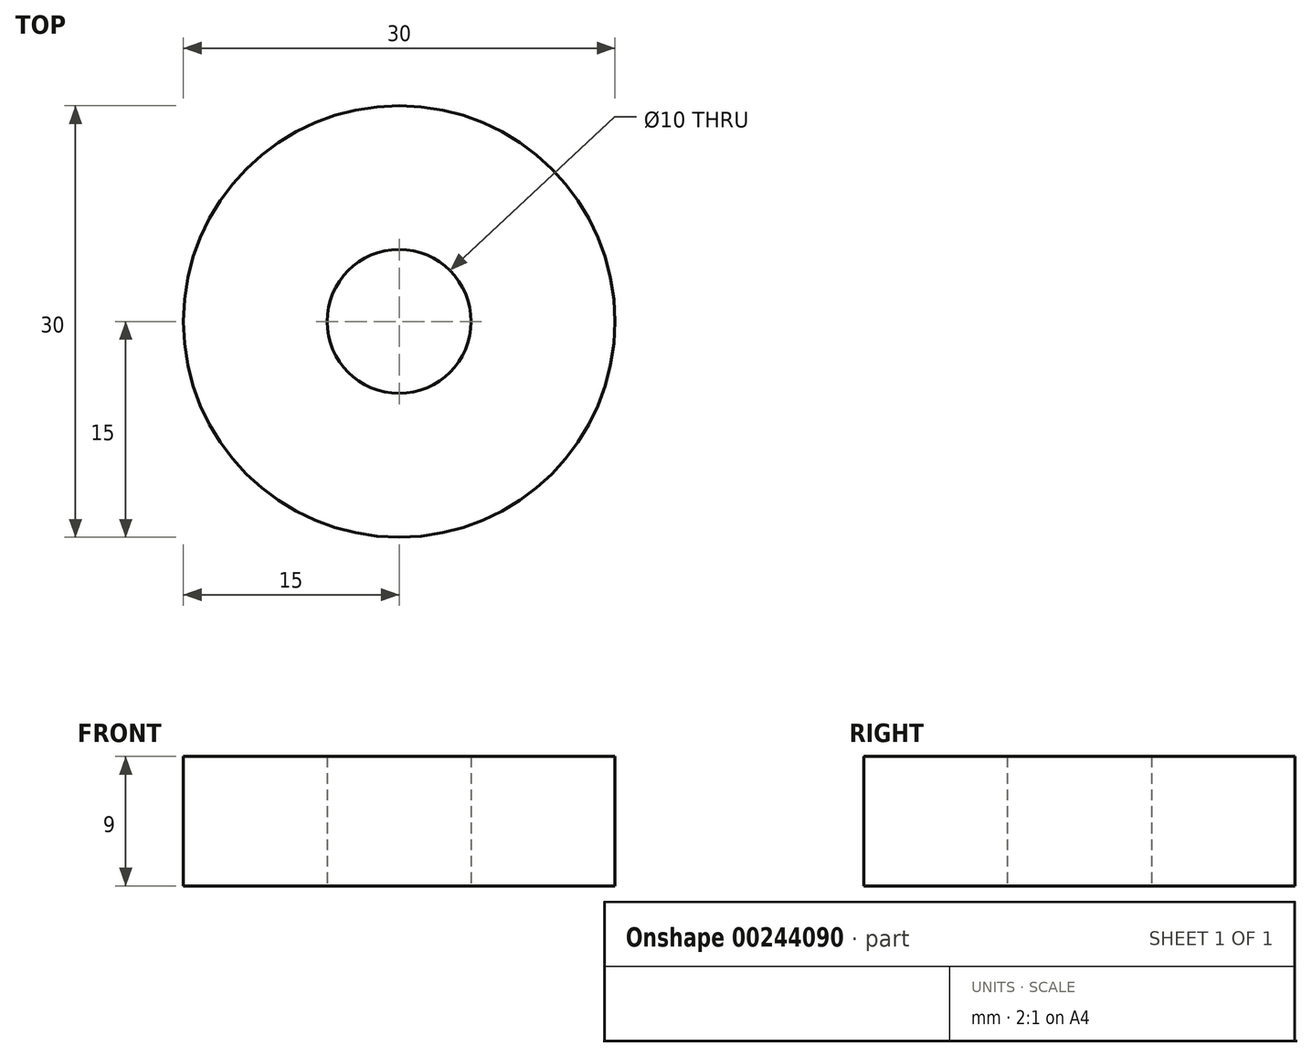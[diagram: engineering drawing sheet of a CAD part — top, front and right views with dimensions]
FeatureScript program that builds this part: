
annotation { "Feature Type Name" : "Feature", "Feature Type Description" : "" }
export const myFeature = defineFeature(function(context is Context, id is Id, definition is map)
    precondition{}
    {
        {
            var Q0;
            Q0=qCreatedBy(makeId("Top.planeOp"),FACE);
            var sketch = newSketch(context, id + "F0", { "sketchPlane" : qUnion([Q0])});
            skCircle(sketch, "E0", {"center": v(0, 0) * mm, "radius": 15 * mm});
            skCircle(sketch, "E1", {"center": v(0, 0) * mm, "radius": 5 * mm});
            skSolve(sketch);
        }
        {
            var Q0;
            Q0 = qSketchRegion(id + "F0", true);
            extrude(context, id + "F1", {"entities" : qUnion([Q0]), "depth" : 9 * mm});
        }
    });
